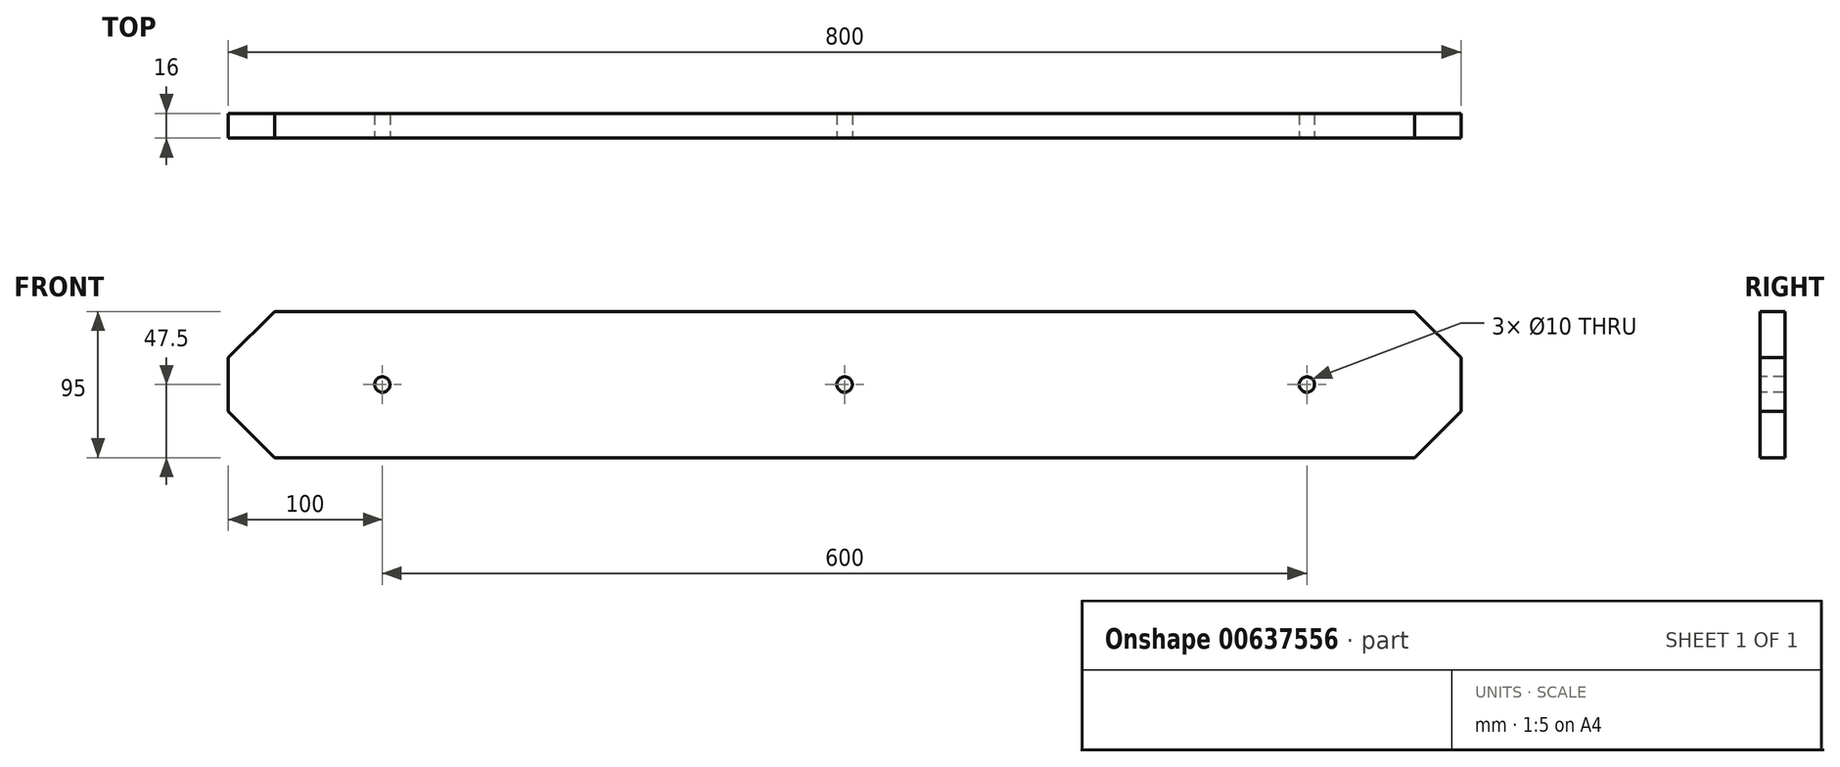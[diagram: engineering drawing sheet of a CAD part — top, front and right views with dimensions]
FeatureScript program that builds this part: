
annotation { "Feature Type Name" : "Feature", "Feature Type Description" : "" }
export const myFeature = defineFeature(function(context is Context, id is Id, definition is map)
    precondition{}
    {
        {
            var Q0;
            Q0=qCreatedBy(makeId("Front.planeOp"),FACE);
            var sketch = newSketch(context, id + "F0", { "sketchPlane" : qUnion([Q0])});
            skLineSegment(sketch, "E0.bottom", {"start": v(-400, 47.5) * mm, "end": v(400, 47.5) * mm});
            skLineSegment(sketch, "E0.top", {"start": v(-400, -47.5) * mm, "end": v(400, -47.5) * mm});
            skLineSegment(sketch, "E0.left", {"start": v(-400, 47.5) * mm, "end": v(-400, -47.5) * mm});
            skLineSegment(sketch, "E0.right", {"start": v(400, 47.5) * mm, "end": v(400, -47.5) * mm});
            skPoint(sketch, "E0.middle", {"position": v(0, 0) * mm});
            skSolve(sketch);
        }
        {
            var Q0;
            Q0=makeQuery(id+"F0.imprint","IMPRINT",FACE,{"disambiguationData":[TD([[makeQuery(id+"F0.imprint","IMPRINT",EDGE,{"derivedFrom":sQuery(id+"F0.wireOp",EDGE,"E0.bottom")}),-1.0]])]});
            extrude(context, id + "F1", {"entities" : qUnion([Q0]), "endBound" : BoundingType.SYMMETRIC, "depth" : 16 * mm, "offsetDistance" : 25 * mm});
        }
        {
            var Q0;
            Q0=makeQuery(id+"F1.opExtrude","SWEPT_EDGE",EDGE,{"disambiguationData":[OSD([sQuery(id+"F0.wireOp",EDGE,"E0.top"),sQuery(id+"F0.wireOp",EDGE,"E0.left")])]});
            var Q1;
            Q1=makeQuery(id+"F1.opExtrude","SWEPT_EDGE",EDGE,{"disambiguationData":[OSD([sQuery(id+"F0.wireOp",EDGE,"E0.bottom"),sQuery(id+"F0.wireOp",EDGE,"E0.left")])]});
            var Q2;
            Q2=makeQuery(id+"F1.opExtrude","SWEPT_EDGE",EDGE,{"disambiguationData":[OSD([sQuery(id+"F0.wireOp",EDGE,"E0.top"),sQuery(id+"F0.wireOp",EDGE,"E0.right")])]});
            var Q3;
            Q3=makeQuery(id+"F1.opExtrude","SWEPT_EDGE",EDGE,{"disambiguationData":[OSD([sQuery(id+"F0.wireOp",EDGE,"E0.bottom"),sQuery(id+"F0.wireOp",EDGE,"E0.right")])]});
            chamfer(context, id + "F2", {"entities" : qUnion([Q0, Q1, Q2, Q3]), "width" : 30 * mm, "tangentPropagation" : true});
        }
        {
            var Q0;
            Q0=makeQuery(id+"F1.opExtrude","CAP_FACE",FACE,{"disambiguationData":[OSD([sQuery(id+"F0.wireOp",EDGE,"E0.bottom"),sQuery(id+"F0.wireOp",EDGE,"E0.top"),sQuery(id+"F0.wireOp",EDGE,"E0.left"),sQuery(id+"F0.wireOp",EDGE,"E0.right")])],"isStart":false});
            var sketch = newSketch(context, id + "F3", { "sketchPlane" : qUnion([Q0])});
            skPoint(sketch, "E1", {"position": v(0, 0) * mm});
            skPoint(sketch, "E2.1.0.0", {"position": v(-300, 0) * mm});
            skLineSegment(sketch, "E2.direction1", {"start": v(0, 0) * mm, "end": v(-300, 0) * mm, "construction": true});
            skPoint(sketch, "E3.1.0.0", {"position": v(300, 0) * mm});
            skLineSegment(sketch, "E3.direction1", {"start": v(0, 0) * mm, "end": v(300, 0) * mm, "construction": true});
            skSolve(sketch);
        }
        {
            var Q0;
            Q0=sQuery(id+"F3.wireOp",VERTEX,"E1");
            var Q1;
            Q1=sQuery(id+"F3.wireOp",VERTEX,"E3.1.0.0");
            var Q2;
            Q2=sQuery(id+"F3.wireOp",VERTEX,"E2.1.0.0");
            var Q3;
            Q3=makeQuery(id+"F1.opExtrude","SWEPT_BODY",BODY,{"disambiguationData":[OSD([sQuery(id+"F0.wireOp",EDGE,"E0.bottom"),sQuery(id+"F0.wireOp",EDGE,"E0.top"),sQuery(id+"F0.wireOp",EDGE,"E0.left"),sQuery(id+"F0.wireOp",EDGE,"E0.right")])]});
            hole(context, id + "F4", {"style" : HoleStyle.SIMPLE, "endStyle" : HoleEndStyle.THROUGH, "holeDiameter" : 10 * mm, "majorDiameter" : 5 * mm, "isTappedThrough" : true, "tappedDepth" : 12 * mm, "tapClearance" : 3, "locations" : qUnion([Q0, Q1, Q2]), "scope" : qUnion([Q3])});
        }
    });
